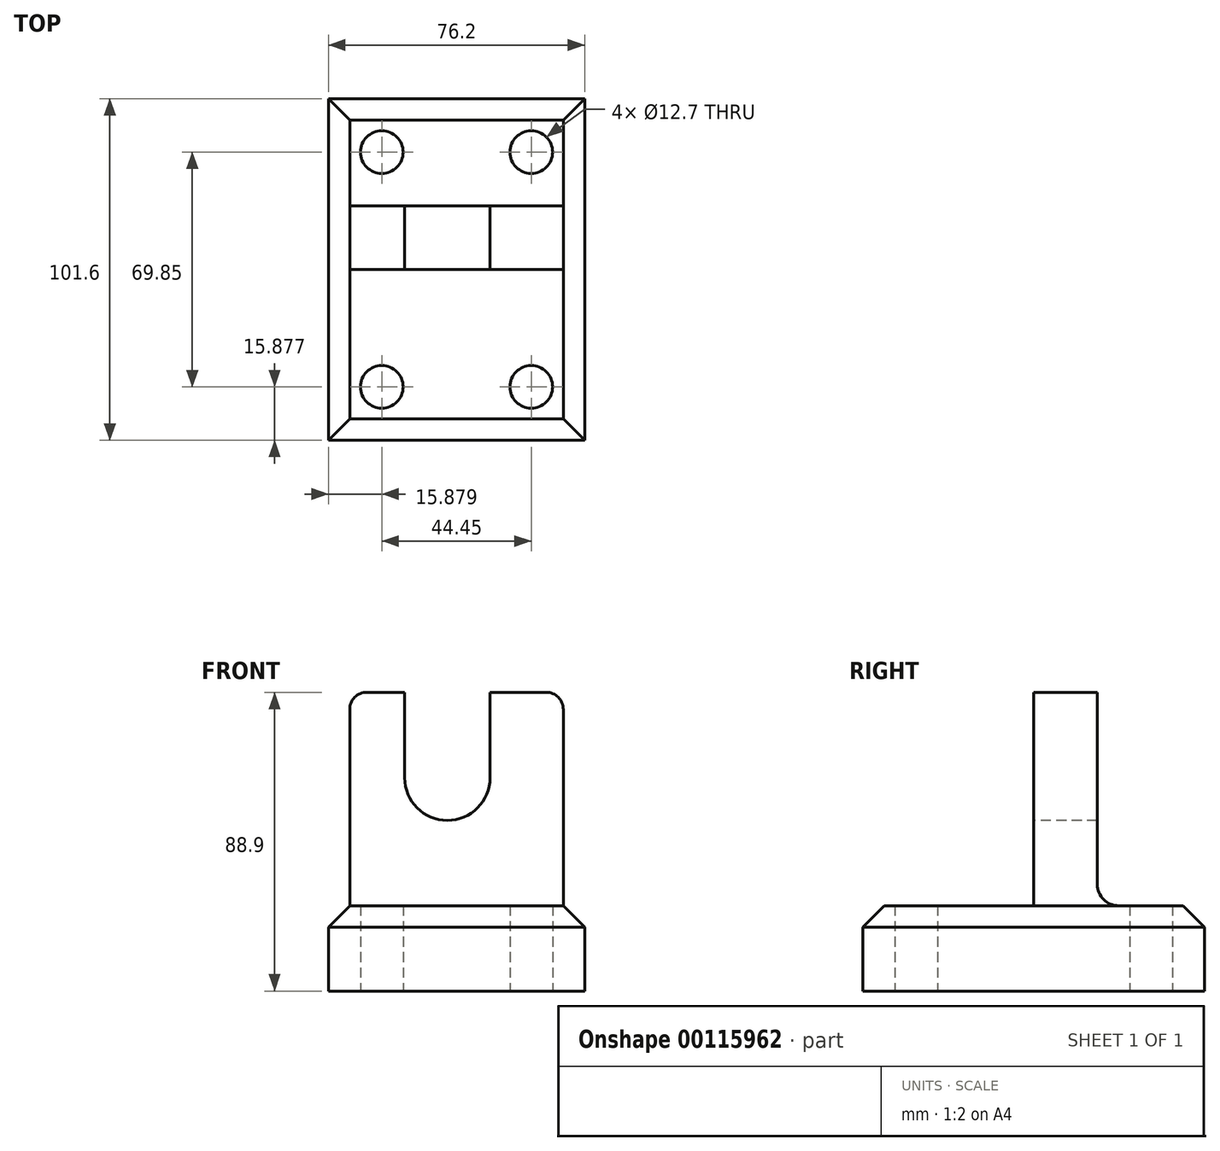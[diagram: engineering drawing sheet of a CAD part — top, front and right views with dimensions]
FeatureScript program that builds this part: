
annotation { "Feature Type Name" : "Feature", "Feature Type Description" : "" }
export const myFeature = defineFeature(function(context is Context, id is Id, definition is map)
    precondition{}
    {
        {
            var Q0;
            Q0=qCreatedBy(makeId("Top.planeOp"),FACE);
            var sketch = newSketch(context, id + "F0", { "sketchPlane" : qUnion([Q0])});
            skLineSegment(sketch, "E0.bottom", {"start": v(-16.85, 76.83) * mm, "end": v(59.35, 76.83) * mm});
            skLineSegment(sketch, "E0.top", {"start": v(-16.85, -24.77) * mm, "end": v(59.35, -24.77) * mm});
            skLineSegment(sketch, "E0.left", {"start": v(-16.85, 76.83) * mm, "end": v(-16.85, -24.77) * mm});
            skLineSegment(sketch, "E0.right", {"start": v(59.35, 76.83) * mm, "end": v(59.35, -24.77) * mm});
            skLineSegment(sketch, "E1.bottom", {"start": v(-16.85, -24.77) * mm, "end": v(-0.97, -24.77) * mm});
            skLineSegment(sketch, "E1.top", {"start": v(-16.85, -8.9) * mm, "end": v(-0.97, -8.9) * mm});
            skLineSegment(sketch, "E1.left", {"start": v(-16.85, -24.77) * mm, "end": v(-16.85, -8.9) * mm});
            skLineSegment(sketch, "E1.right", {"start": v(-0.97, -24.77) * mm, "end": v(-0.97, -8.9) * mm});
            skCircle(sketch, "E2", {"center": v(-0.97, -8.9) * mm, "radius": 6.35 * mm});
            skLineSegment(sketch, "E3.bottom", {"start": v(59.35, -24.77) * mm, "end": v(43.48, -24.77) * mm});
            skLineSegment(sketch, "E3.top", {"start": v(59.35, -8.9) * mm, "end": v(43.48, -8.9) * mm});
            skLineSegment(sketch, "E3.left", {"start": v(59.35, -24.77) * mm, "end": v(59.35, -8.9) * mm});
            skLineSegment(sketch, "E3.right", {"start": v(43.48, -24.77) * mm, "end": v(43.48, -8.9) * mm});
            skCircle(sketch, "E4", {"center": v(43.48, -8.9) * mm, "radius": 6.35 * mm});
            skLineSegment(sketch, "E5", {"start": v(-0.97, -24.77) * mm, "end": v(43.48, -24.77) * mm});
            skLineSegment(sketch, "E6.bottom", {"start": v(59.35, 76.83) * mm, "end": v(43.48, 76.83) * mm});
            skLineSegment(sketch, "E6.top", {"start": v(59.35, 60.96) * mm, "end": v(43.48, 60.96) * mm});
            skLineSegment(sketch, "E6.left", {"start": v(59.35, 76.83) * mm, "end": v(59.35, 60.96) * mm});
            skLineSegment(sketch, "E6.right", {"start": v(43.48, 76.83) * mm, "end": v(43.48, 60.96) * mm});
            skLineSegment(sketch, "E7.bottom", {"start": v(-16.85, 76.83) * mm, "end": v(-0.97, 76.83) * mm});
            skLineSegment(sketch, "E7.top", {"start": v(-16.85, 60.96) * mm, "end": v(-0.97, 60.96) * mm});
            skLineSegment(sketch, "E7.left", {"start": v(-16.85, 76.83) * mm, "end": v(-16.85, 60.96) * mm});
            skLineSegment(sketch, "E7.right", {"start": v(-0.97, 76.83) * mm, "end": v(-0.97, 60.96) * mm});
            skCircle(sketch, "E8", {"center": v(-0.97, 60.96) * mm, "radius": 6.35 * mm});
            skCircle(sketch, "E9", {"center": v(43.48, 60.96) * mm, "radius": 6.35 * mm});
            skLineSegment(sketch, "E10.top", {"start": v(-16.85, 26.03) * mm, "end": v(59.35, 26.03) * mm});
            skLineSegment(sketch, "E10.left", {"start": v(-16.85, -24.77) * mm, "end": v(-16.85, 26.03) * mm});
            skLineSegment(sketch, "E10.right", {"start": v(59.35, -24.77) * mm, "end": v(59.35, 26.03) * mm});
            skLineSegment(sketch, "E11.top", {"start": v(-16.85, 45.08) * mm, "end": v(59.35, 45.08) * mm});
            skLineSegment(sketch, "E11.left", {"start": v(-16.85, 26.03) * mm, "end": v(-16.85, 45.08) * mm});
            skLineSegment(sketch, "E11.right", {"start": v(59.35, 26.03) * mm, "end": v(59.35, 45.08) * mm});
            skSolve(sketch);
        }
        {
            var Q0;
            Q0=qSketchRegion(id+"F0",true);
            extrude(context, id + "F1", {"entities" : qUnion([Q0]), "depth" : 25.4 * mm});
        }
        {
            var Q0;
            Q0=makeQuery(id+"F1.opExtrude","CAP_EDGE",EDGE,{"disambiguationData":[OSD([sQuery(id+"F0.wireOp",EDGE,"E0.left"),sQuery(id+"F0.wireOp",EDGE,"E7.left"),sQuery(id+"F0.wireOp",EDGE,"E10.left"),sQuery(id+"F0.wireOp",EDGE,"E11.left")])],"isStart":false});
            var Q1;
            Q1=makeQuery(id+"F1.opExtrude","CAP_EDGE",EDGE,{"disambiguationData":[OSD([sQuery(id+"F0.wireOp",EDGE,"E0.top")])],"isStart":false});
            var Q2;
            Q2=makeQuery(id+"F1.opExtrude","CAP_EDGE",EDGE,{"disambiguationData":[OSD([sQuery(id+"F0.wireOp",EDGE,"E0.right"),sQuery(id+"F0.wireOp",EDGE,"E6.left"),sQuery(id+"F0.wireOp",EDGE,"E10.right"),sQuery(id+"F0.wireOp",EDGE,"E11.right")])],"isStart":false});
            var Q3;
            Q3=makeQuery(id+"F1.opExtrude","CAP_EDGE",EDGE,{"disambiguationData":[OSD([sQuery(id+"F0.wireOp",EDGE,"E0.bottom"),sQuery(id+"F0.wireOp",EDGE,"E6.bottom"),sQuery(id+"F0.wireOp",EDGE,"E7.bottom")])],"isStart":false});
            chamfer(context, id + "F2", {"entities" : qUnion([Q0, Q1, Q2, Q3]), "width" : 6.35 * mm, "tangentPropagation" : true});
        }
        {
            var Q0;
            Q0=makeQuery(id+"F1.opExtrude","CAP_FACE",FACE,{"disambiguationData":[OSD([sQuery(id+"F0.wireOp",EDGE,"E0.bottom"),sQuery(id+"F0.wireOp",EDGE,"E0.left"),sQuery(id+"F0.wireOp",EDGE,"E0.right"),sQuery(id+"F0.wireOp",EDGE,"E2"),sQuery(id+"F0.wireOp",EDGE,"E4"),sQuery(id+"F0.wireOp",EDGE,"E6.bottom"),sQuery(id+"F0.wireOp",EDGE,"E6.left"),sQuery(id+"F0.wireOp",EDGE,"E7.bottom"),sQuery(id+"F0.wireOp",EDGE,"E7.left"),sQuery(id+"F0.wireOp",EDGE,"E8"),sQuery(id+"F0.wireOp",EDGE,"E9"),sQuery(id+"F0.wireOp",EDGE,"E0.top"),sQuery(id+"F0.wireOp",EDGE,"E10.left"),sQuery(id+"F0.wireOp",EDGE,"E10.right"),sQuery(id+"F0.wireOp",EDGE,"E11.left"),sQuery(id+"F0.wireOp",EDGE,"E11.right")])],"isStart":false});
            var sketch = newSketch(context, id + "F3", { "sketchPlane" : qUnion([Q0])});
            skLineSegment(sketch, "E12.bottom", {"start": v(-10.5, 44.97) * mm, "end": v(53, 44.97) * mm});
            skLineSegment(sketch, "E12.top", {"start": v(-10.5, 26.03) * mm, "end": v(53, 26.03) * mm});
            skLineSegment(sketch, "E12.left", {"start": v(-10.5, 44.97) * mm, "end": v(-10.5, 26.03) * mm});
            skLineSegment(sketch, "E12.right", {"start": v(53, 44.97) * mm, "end": v(53, 26.03) * mm});
            skSolve(sketch);
        }
        {
            var Q0;
            Q0=qSketchRegion(id+"F3",true);
            extrude(context, id + "F4", {"entities" : qUnion([Q0]), "operationType" : NewBodyOperationType.ADD, "depth" : 63.5 * mm});
        }
        {
            var Q0;
            Q0=makeQuery(id+"F4.opExtrude","SWEPT_FACE",FACE,{"disambiguationData":[OSD([sQuery(id+"F3.wireOp",EDGE,"E12.top")])]});
            var sketch = newSketch(context, id + "F5", { "sketchPlane" : qUnion([Q0])});
            skLineSegment(sketch, "E13", {"start": v(53, 25.4) * mm, "end": v(53, 63.5) * mm});
            skLineSegment(sketch, "E14", {"start": v(53, 63.5) * mm, "end": v(18.53, 63.5) * mm});
            skCircle(sketch, "E15", {"center": v(18.53, 63.5) * mm, "radius": 9.53 * mm});
            skCircle(sketch, "E16", {"center": v(18.53, 63.5) * mm, "radius": 15.88 * mm});
            skSolve(sketch);
        }
        {
            var Q0;
            Q0=sQuery(id+"F5.wireOp",VERTEX,"E14.end");
            var Q1;
            Q1=makeQuery(id+"F1.opExtrude","SWEPT_BODY",BODY,{"disambiguationData":[OSD([sQuery(id+"F0.wireOp",EDGE,"E0.bottom"),sQuery(id+"F0.wireOp",EDGE,"E0.left"),sQuery(id+"F0.wireOp",EDGE,"E0.right"),sQuery(id+"F0.wireOp",EDGE,"E2"),sQuery(id+"F0.wireOp",EDGE,"E4"),sQuery(id+"F0.wireOp",EDGE,"E6.bottom"),sQuery(id+"F0.wireOp",EDGE,"E6.left"),sQuery(id+"F0.wireOp",EDGE,"E7.bottom"),sQuery(id+"F0.wireOp",EDGE,"E7.left"),sQuery(id+"F0.wireOp",EDGE,"E8"),sQuery(id+"F0.wireOp",EDGE,"E9"),sQuery(id+"F0.wireOp",EDGE,"E0.top"),sQuery(id+"F0.wireOp",EDGE,"E10.left"),sQuery(id+"F0.wireOp",EDGE,"E10.right"),sQuery(id+"F0.wireOp",EDGE,"E11.left"),sQuery(id+"F0.wireOp",EDGE,"E11.right")])]});
            hole(context, id + "F6", {"style" : HoleStyle.SIMPLE, "endStyle" : HoleEndStyle.THROUGH, "holeDiameter" : 25.4 * mm, "locations" : qUnion([Q0]), "scope" : qUnion([Q1]), "isTappedThrough" : true});
        }
        {
            var Q0;
            Q0=makeQuery(id+"F4.opExtrude","SWEPT_FACE",FACE,{"disambiguationData":[OSD([sQuery(id+"F3.wireOp",EDGE,"E12.top")])]});
            var sketch = newSketch(context, id + "F7", { "sketchPlane" : qUnion([Q0])});
            skLineSegment(sketch, "E17", {"start": v(5.83, 63.5) * mm, "end": v(5.83, 88.9) * mm});
            skLineSegment(sketch, "E18", {"start": v(31.23, 63.5) * mm, "end": v(31.23, 88.9) * mm});
            skSolve(sketch);
        }
        {
            var Q0;
            {var subQ0=sQuery(id+"F7.wireOp",EDGE,"E17");Q0=makeQuery(id+"F7.imprint","IMPRINT",FACE,{"disambiguationData":[TD([[makeQuery(id+"F7.imprint","IMPRINT",EDGE,{"derivedFrom":subQ0}),-1.0]])]});}
            extrude(context, id + "F8", {"entities" : qUnion([Q0]), "operationType" : NewBodyOperationType.REMOVE, "oppositeDirection" : true, "depth" : 25.4 * mm});
        }
        {
            var Q0;
            Q0=makeQuery(id+"F4.opExtrude","CAP_EDGE",EDGE,{"disambiguationData":[OSD([sQuery(id+"F3.wireOp",EDGE,"E12.top")])],"isStart":true});
            var Q1;
            Q1=makeQuery(id+"F4.opExtrude","CAP_EDGE",EDGE,{"disambiguationData":[OSD([sQuery(id+"F3.wireOp",EDGE,"E12.bottom")])],"isStart":true});
            fillet(context, id + "F9", {"entities" : qUnion([Q0, Q1]), "radius" : 6.35 * mm, "tangentPropagation" : true, "allowEdgeOverflow" : false});
        }
        {
            var Q0;
            Q0=makeQuery(id+"F4.opExtrude","CAP_EDGE",EDGE,{"disambiguationData":[OSD([sQuery(id+"F3.wireOp",EDGE,"E12.left")])],"isStart":false});
            var Q1;
            Q1=makeQuery(id+"F4.opExtrude","CAP_EDGE",EDGE,{"disambiguationData":[OSD([sQuery(id+"F3.wireOp",EDGE,"E12.right")])],"isStart":false});
            fillet(context, id + "F10", {"entities" : qUnion([Q0, Q1]), "radius" : 5.08 * mm, "tangentPropagation" : true, "allowEdgeOverflow" : false});
        }
    });
